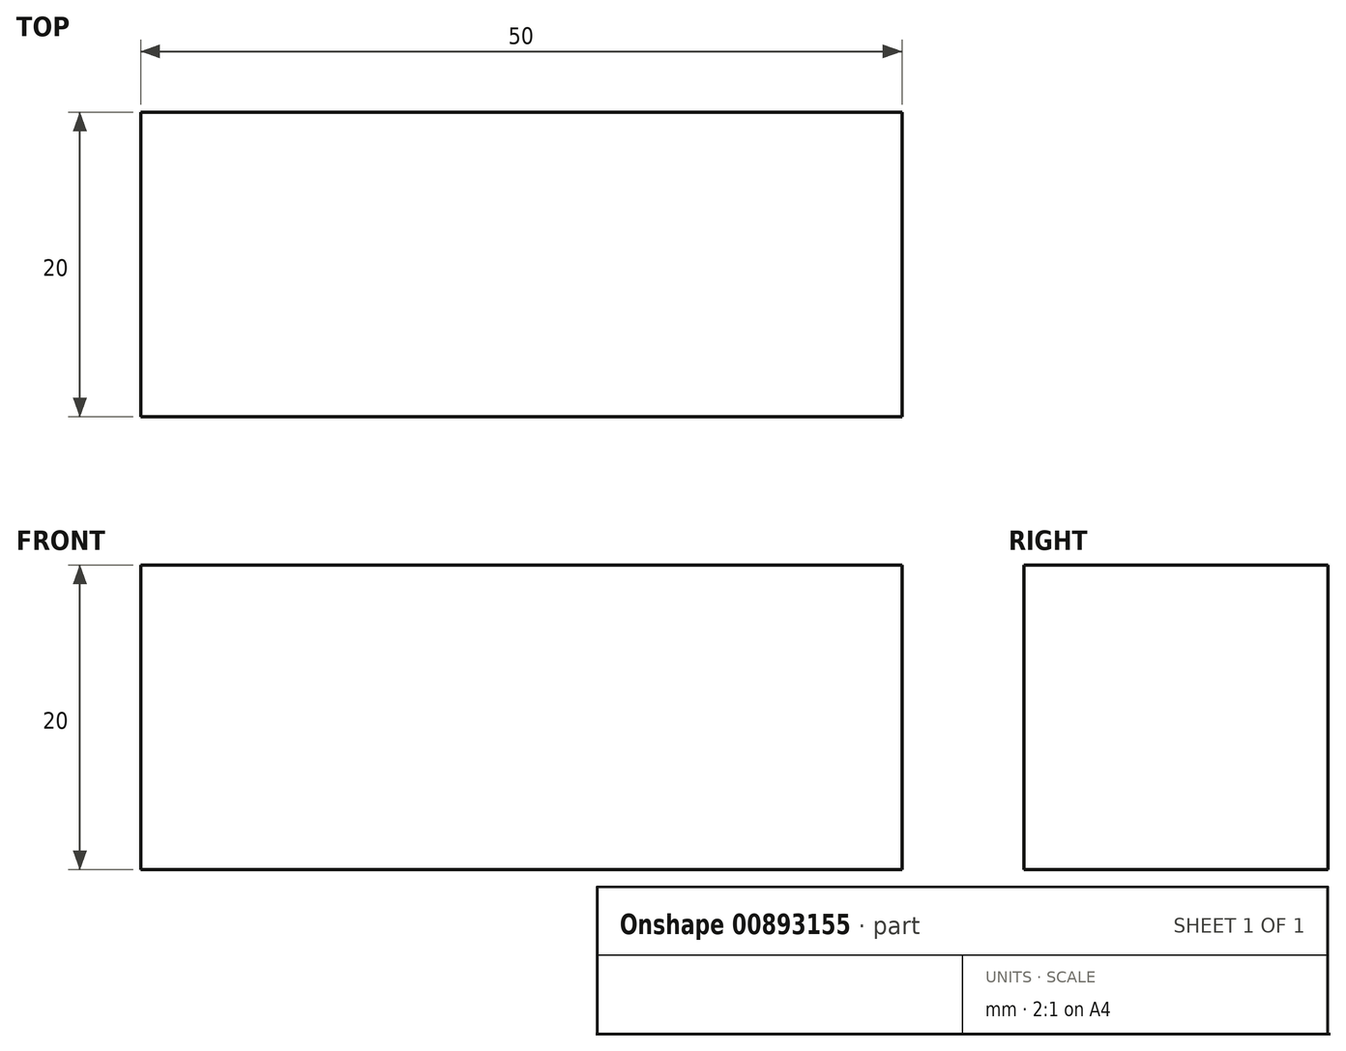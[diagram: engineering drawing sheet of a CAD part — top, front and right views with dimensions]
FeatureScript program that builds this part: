
annotation { "Feature Type Name" : "Feature", "Feature Type Description" : "" }
export const myFeature = defineFeature(function(context is Context, id is Id, definition is map)
    precondition{}
    {
        {
            var Q0;
            Q0=qCreatedBy(makeId("Top.planeOp"),FACE);
            var sketch = newSketch(context, id + "F0", { "sketchPlane" : qUnion([Q0])});
            skLineSegment(sketch, "E0.bottom", {"start": v(-20.54, 9.56) * mm, "end": v(29.46, 9.56) * mm});
            skLineSegment(sketch, "E0.top", {"start": v(-20.54, -10.44) * mm, "end": v(29.46, -10.44) * mm});
            skLineSegment(sketch, "E0.left", {"start": v(-20.54, 9.56) * mm, "end": v(-20.54, -10.44) * mm});
            skLineSegment(sketch, "E0.right", {"start": v(29.46, 9.56) * mm, "end": v(29.46, -10.44) * mm});
            skSolve(sketch);
        }
        {
            var Q0;
            Q0 = qSketchRegion(id + "F0", true);
            extrude(context, id + "F1", {"entities" : qUnion([Q0]), "depth" : 20 * mm, "offsetDistance" : 25 * mm});
        }
    });
